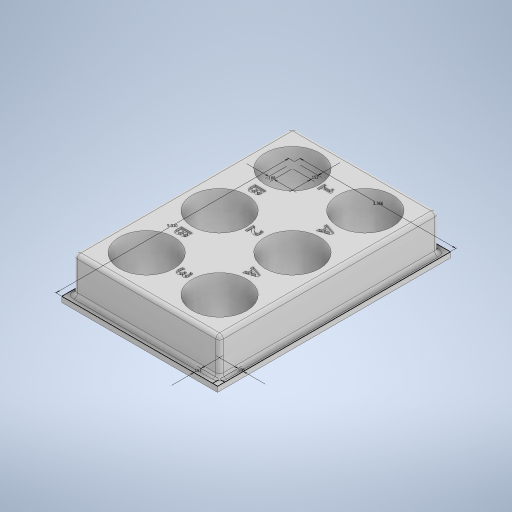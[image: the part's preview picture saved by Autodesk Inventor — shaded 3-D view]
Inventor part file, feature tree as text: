
AUTODESK INVENTOR PART (.ipt)
format: ipt  version: 2024.1 (Build 281209000, 209)  size: 752,640 bytes
history: native  units: in
note: dims shown in document units (in); Inventor stores cm internally (conversion verified against a paired STEP export)
features: extrude x6, fillet x3, sketch x2
ambient origin geometry x8: Origin, YZ Plane, XZ Plane, XY Plane, X Axis, Y Axis, Z Axis, Center Point
bodies: Solid1 (feature_tree)
feature tree (11):
  extrude  "Extrusion1"  Depth=5.0295in
  extrude  "Extrusion2"  Depth=0.1526in
  extrude  "Extrusion3"  Depth=0.1083in
  extrude  "Extrusion4"  Depth=0.1526in
  fillet  "Fillet1"  Radius=0.7874in
  fillet  "Fillet2"  Radius=0.1181in
  fillet  "Fillet3"  Radius=0.7874in
  extrude  "Extrusion5"  Depth=0.7874in
  extrude  "Extrusion6"  Depth=1.1811in
  sketch  "Sketch4"  dims[d0=3.3661in d1=5.0295in]
  sketch  "Sketch5"  dims[d2=0.1083in d3=0.1526in d4=0.1083in d5=0.1526in d6=0.7874in d7=0.0in d8=0.1181in d9=0.0in d10=0.7874in d11=0.7874in d12=1.1811in d13=0.7874in d15=1.5748in d16=1.1811in d18=1.5748in d21=0.7874in d22=0.0in d23=1.2992in d24=0.7874in d26=1.5748in d27=1.1811in d29=1.5748in d32=0.1181in d33=0.1181in d34=0.1181in d35=0.1181in d36=0.7087in d37=0.0in d38=0.125in d39=0.125in d40=0.0787in d41=0.0394in d42=0.0in d43=0.0in d44=0.0in]
